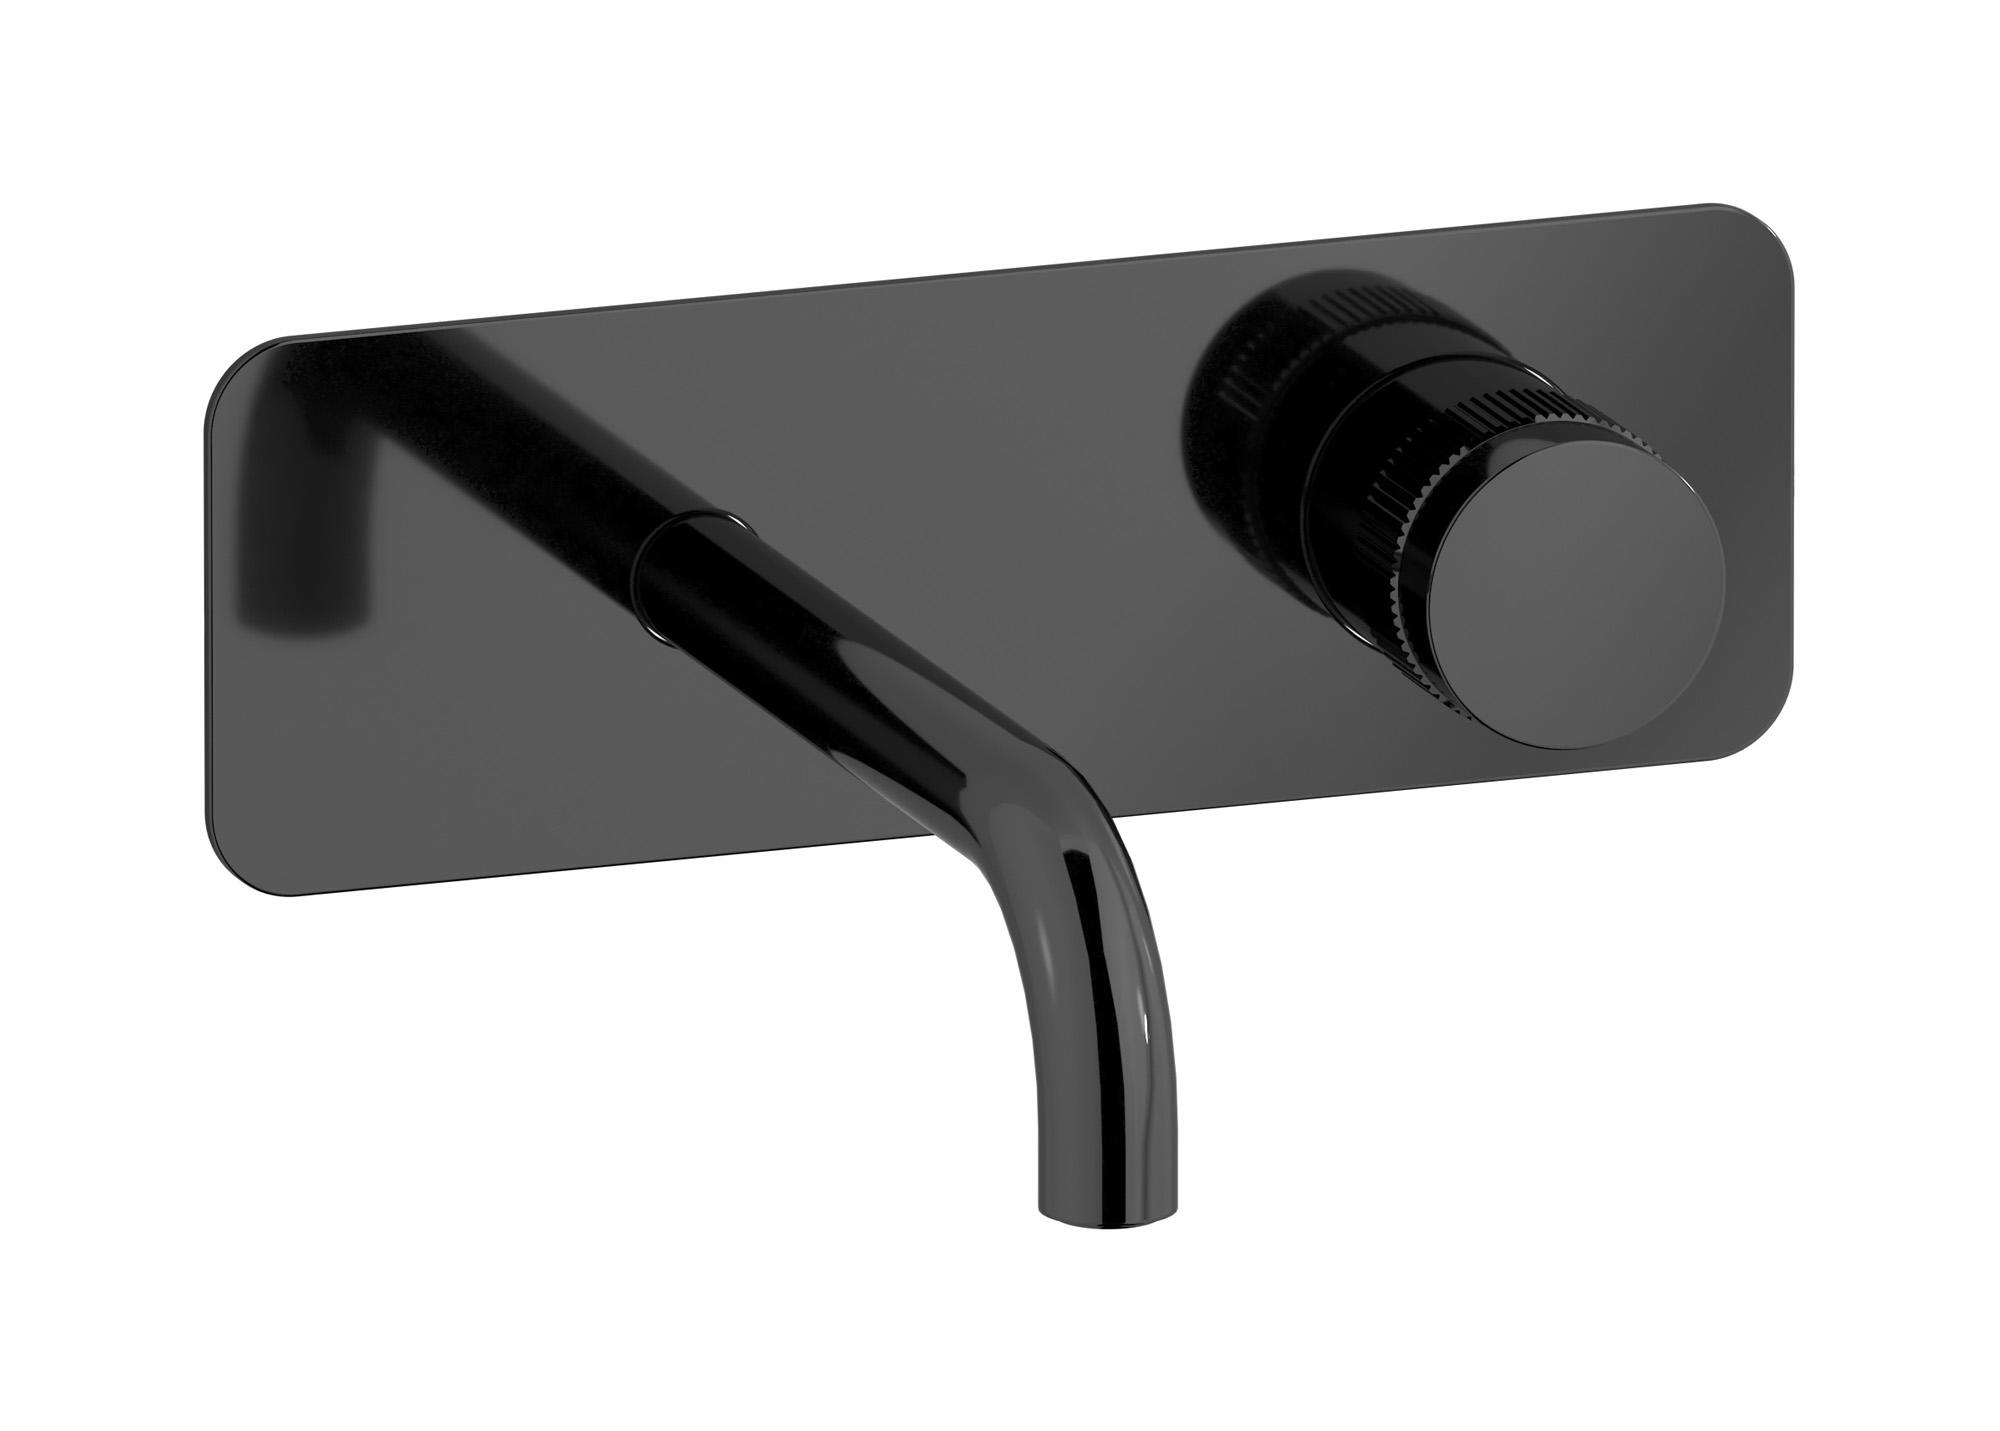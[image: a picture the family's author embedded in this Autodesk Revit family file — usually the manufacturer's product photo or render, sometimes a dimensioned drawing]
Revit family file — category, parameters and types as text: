
# Revit family: RX206
name_source: partatom
category: Apparecchi idraulici
units: mm (PartAtom-declared; Revit-internal decimal feet)

## family parameters
Basato su piano di lavoro = No
Condiviso = No
Mantieni orientamento annotazione = No
Numero OmniClass = 23.45.55.17
Punto di calcolo locali = No
Quota connettore circolare = Usa diametro
Sempre verticale = Sì
Taglio con vuoti quando caricato = No
Tipo di parte = Normale
Titolo OmniClass = Mixing Faucets

## types (12) — shared parameters
Cold water inlet = 10 mm  [stored 0.0328084 ft]
Commenti sul tipo = Wall monted washbasin hydroprogressive mixer complete with drain
Connessione CW = No
Connessione HW = No
Connessione di scarico = No
Connessione di ventilazione = No
Descrizione = Wall monted washbasin hydroprogressive mixer complete with drain
Hot water inlet = 10 mm  [stored 0.0328084 ft]
Produttore = IB Rubinetterie S.p.A.
URL = https://www.weareib.it
zero-valued in all types: Prospetto di default

## per-type parameters (varying)
| type | Finishes surface | Immagine tipo | Modello |
| Chrome | IB_Chrome | RX206CC.jpg | RX206CC |
| Black Chrome | IB_Black chrome | RX206CF.jpg | RX206CF |
| Brushed Black Chrome | IB_Brushed black chrome | RX206CS.jpg | RX206CS |
| Pale Gold | IB_Pale gold | RX206II.jpg | RX206II |
| Brushed Pale Gold | IB_brushed pale gold | RX206IS.jpg | RX206IS |
| Matt Black | IB_matt black | RX206NP.jpg | RX206NP |
| Natural Brass | IB_Brass | RX206ON.jpg | RX206ON |
| Gold | IB_gold | RX206OO.jpg | RX206OO |
| Brushed Gold | IB_brushed gold | RX206OS.jpg | RX206OS |
| Rose Gold | IB_Rose gold | RX206RS.jpg | RX206RS |
| Brushed Rose Gold | IB_Brushed rose gold | RX206SR.jpg | RX206SR |
| Brushed Nickel | IB_Brushed nickel | RX206SS.jpg | RX206SS |

note: [stored X ft] marks values corroborated as IEEE doubles in the binary element streams (Revit-internal decimal feet)
